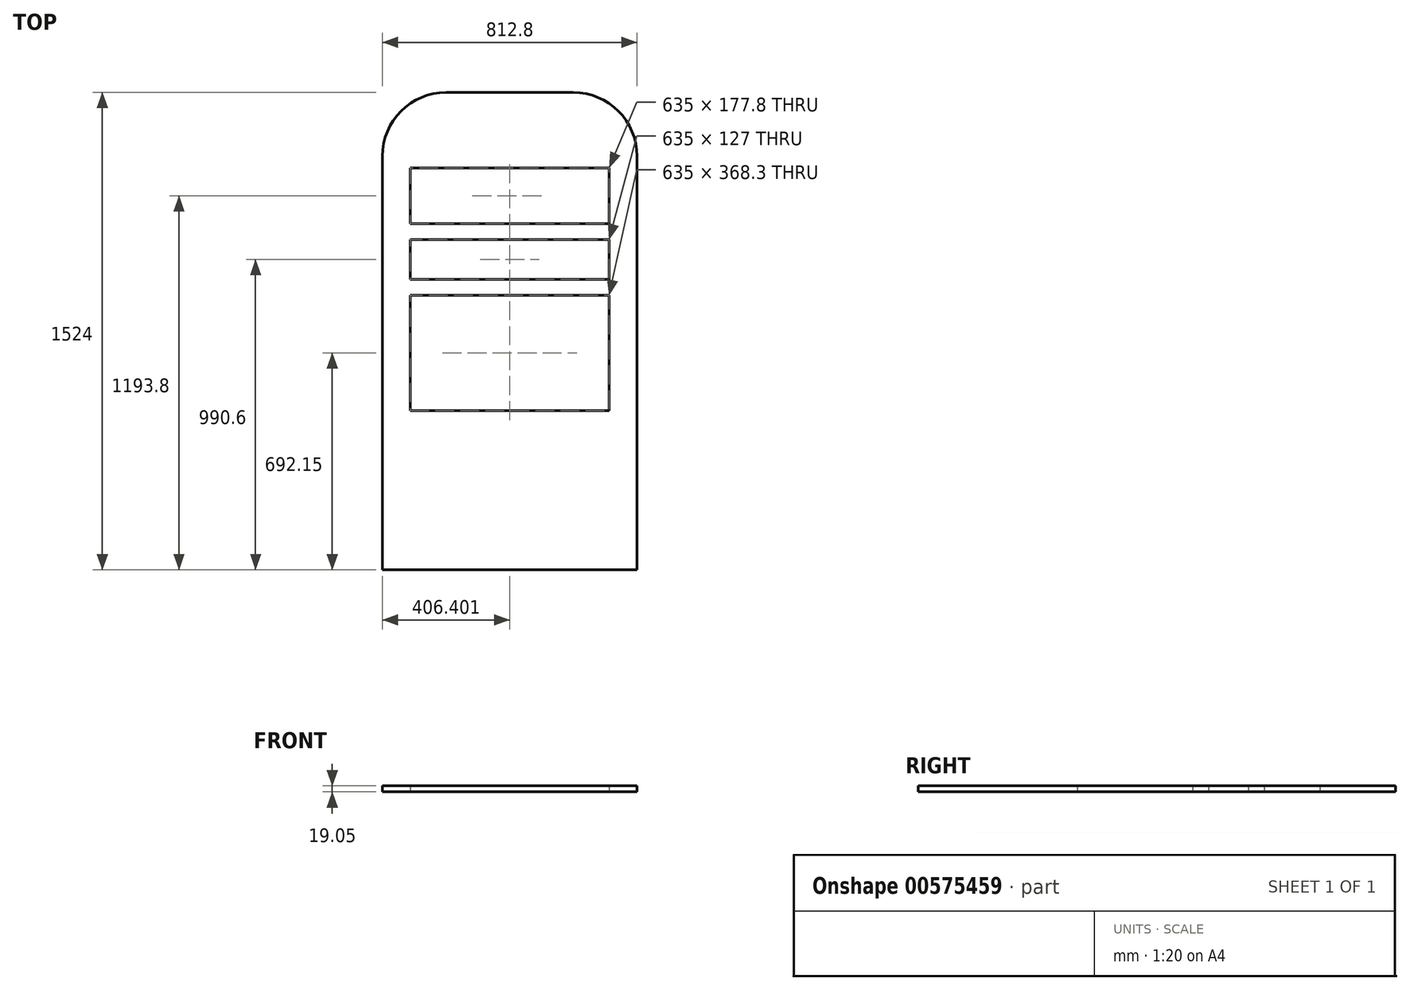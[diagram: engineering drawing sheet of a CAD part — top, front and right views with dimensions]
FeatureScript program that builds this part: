
annotation { "Feature Type Name" : "Feature", "Feature Type Description" : "" }
export const myFeature = defineFeature(function(context is Context, id is Id, definition is map)
    precondition{}
    {
        {
            var Q0;
            Q0=qCreatedBy(makeId("Top.planeOp"),FACE);
            var sketch = newSketch(context, id + "F0", { "sketchPlane" : qUnion([Q0])});
            skLineSegment(sketch, "E0.top", {"start": v(-648.04, -556.98) * mm, "end": v(164.76, -556.98) * mm});
            skLineSegment(sketch, "E0.left", {"start": v(-648.04, 763.82) * mm, "end": v(-648.04, -556.98) * mm});
            skLineSegment(sketch, "E0.right", {"start": v(164.76, 763.82) * mm, "end": v(164.76, -556.98) * mm});
            skLineSegment(sketch, "E1.0", {"start": v(-559.14, -48.98) * mm, "end": v(75.86, -48.98) * mm});
            skLineSegment(sketch, "E2.0", {"start": v(-559.14, 725.72) * mm, "end": v(-559.14, 547.92) * mm});
            skLineSegment(sketch, "E3.0", {"start": v(-559.14, 725.72) * mm, "end": v(75.86, 725.72) * mm});
            skLineSegment(sketch, "E4.0", {"start": v(75.86, 725.72) * mm, "end": v(75.86, 547.92) * mm});
            skLineSegment(sketch, "E5.0", {"start": v(-559.14, 319.32) * mm, "end": v(75.86, 319.32) * mm});
            skLineSegment(sketch, "E6.trimOffspring", {"start": v(-559.14, 90.72) * mm, "end": v(-559.14, -48.98) * mm});
            skLineSegment(sketch, "E7.trimOffspring", {"start": v(75.86, 90.72) * mm, "end": v(75.86, -48.98) * mm});
            skLineSegment(sketch, "E8.trimOffspring", {"start": v(75.86, 319.32) * mm, "end": v(75.86, 141.52) * mm});
            skLineSegment(sketch, "E9.trimOffspring", {"start": v(-559.14, 319.32) * mm, "end": v(-559.14, 141.52) * mm});
            skLineSegment(sketch, "E10.trimOffspring", {"start": v(-559.14, 497.12) * mm, "end": v(-559.14, 370.12) * mm});
            skLineSegment(sketch, "E11.trimOffspring", {"start": v(75.86, 497.12) * mm, "end": v(75.86, 370.12) * mm});
            skLineSegment(sketch, "E12", {"start": v(-559.14, 370.12) * mm, "end": v(75.86, 370.12) * mm});
            skLineSegment(sketch, "E13", {"start": v(-559.14, 90.72) * mm, "end": v(-559.14, 141.52) * mm});
            skLineSegment(sketch, "E14", {"start": v(75.86, 90.72) * mm, "end": v(75.86, 141.52) * mm});
            skLineSegment(sketch, "E15", {"start": v(-559.14, 547.92) * mm, "end": v(75.86, 547.92) * mm});
            skLineSegment(sketch, "E16", {"start": v(75.86, 497.12) * mm, "end": v(-559.14, 497.12) * mm});
            skLineSegment(sketch, "E17", {"start": v(-444.84, 967.02) * mm, "end": v(-38.44, 967.02) * mm});
            skPoint(sketch, "E18.visualSharp", {"position": v(-648.04, 967.02) * mm});
            skArc(sketch, "E18.filletArc", {"start": v(-444.84, 967.02) * mm, "mid": v(-588.52, 907.5) * mm, "end": v(-648.04, 763.82) * mm});
            skPoint(sketch, "E19.visualSharp", {"position": v(164.76, 967.02) * mm});
            skArc(sketch, "E19.filletArc", {"start": v(164.76, 763.82) * mm, "mid": v(105.25, 907.5) * mm, "end": v(-38.44, 967.02) * mm});
            skPoint(sketch, "E20.startSnap0", {"position": v(-241.64, 643.17) * mm});
            skPoint(sketch, "E21.startSnap0", {"position": v(-241.64, -302.98) * mm});
            skSolve(sketch);
        }
        {
            var Q0;
            Q0=makeQuery(id+"F0.imprint","IMPRINT",FACE,{"disambiguationData":[TD([[makeQuery(id+"F0.imprint","IMPRINT",EDGE,{"derivedFrom":sQuery(id+"F0.wireOp",EDGE,"E0.top")}),1.0]])]});
            extrude(context, id + "F1", {"entities" : qUnion([Q0]), "depth" : 19.05 * mm, "offsetDistance" : 25.4 * mm});
        }
    });
